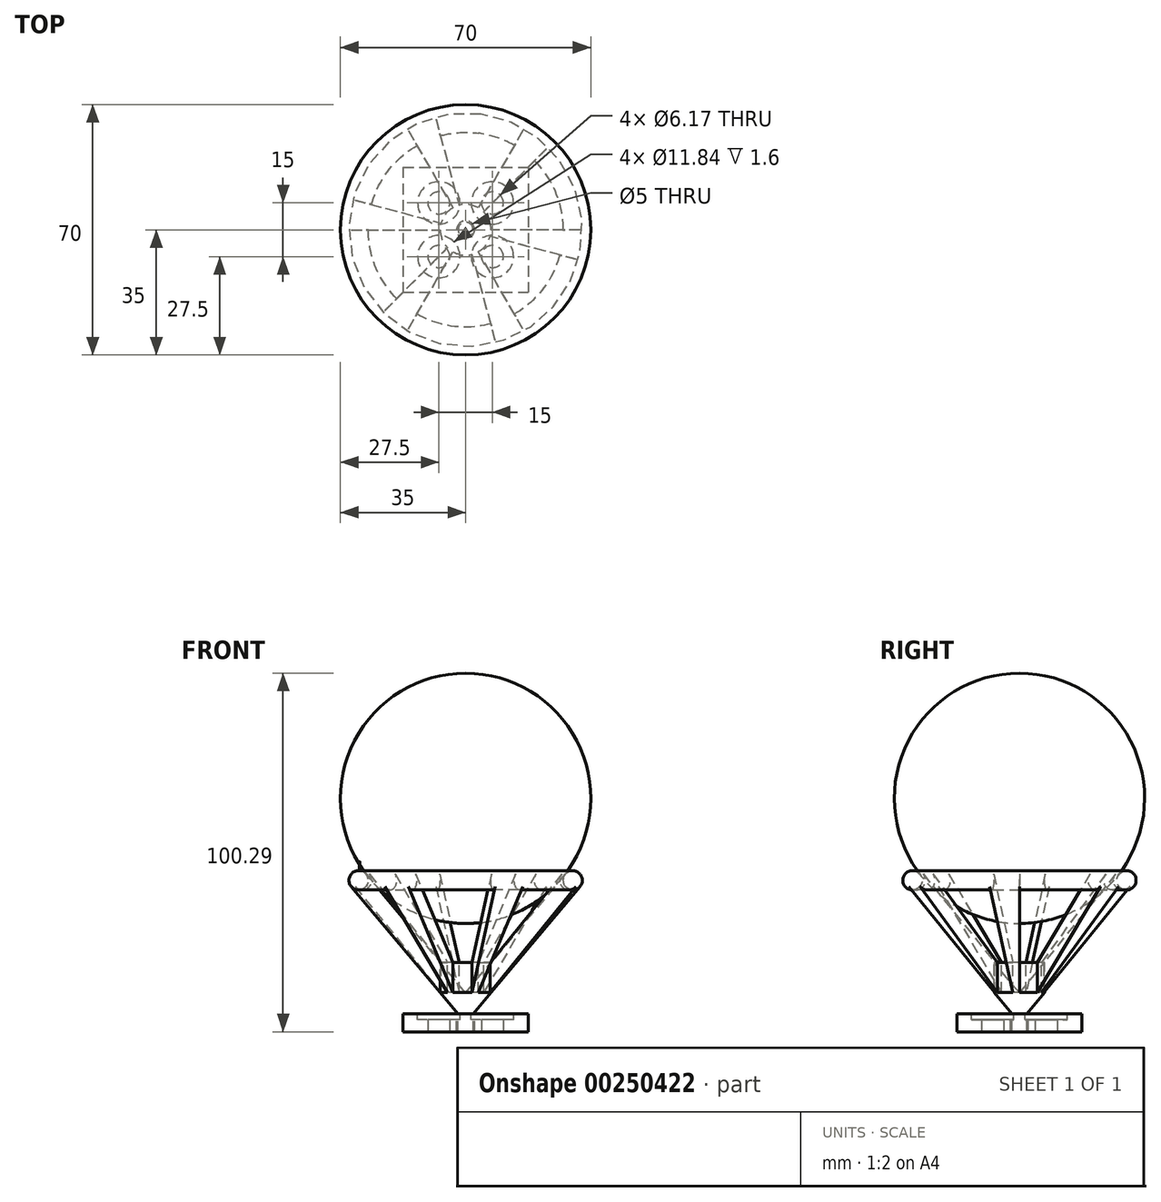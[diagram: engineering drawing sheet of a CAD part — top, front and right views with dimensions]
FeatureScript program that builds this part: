
annotation { "Feature Type Name" : "Feature", "Feature Type Description" : "" }
export const myFeature = defineFeature(function(context is Context, id is Id, definition is map)
    precondition{}
    {
        {
            var Q0;
            Q0=qCreatedBy(makeId("Top.planeOp"),FACE);
            var sketch = newSketch(context, id + "F0", { "sketchPlane" : qUnion([Q0])});
            skLineSegment(sketch, "E0.bottom", {"start": v(-17.5, 17.5) * mm, "end": v(0, 17.5) * mm});
            skLineSegment(sketch, "E0.top", {"start": v(-17.5, -17.5) * mm, "end": v(0, -17.5) * mm});
            skLineSegment(sketch, "E0.left", {"start": v(-17.5, 17.5) * mm, "end": v(-17.5, 0) * mm});
            skLineSegment(sketch, "E0.right", {"start": v(17.5, 17.5) * mm, "end": v(17.5, 0) * mm});
            skLineSegment(sketch, "E1", {"start": v(-17.5, 0) * mm, "end": v(-17.5, -17.5) * mm});
            skLineSegment(sketch, "E2", {"start": v(17.5, 0) * mm, "end": v(17.5, -17.5) * mm});
            skLineSegment(sketch, "E3", {"start": v(0, -17.5) * mm, "end": v(17.5, -17.5) * mm});
            skLineSegment(sketch, "E4", {"start": v(0, 17.5) * mm, "end": v(17.5, 17.5) * mm});
            skCircle(sketch, "E5", {"center": v(-7.5, 7.5) * mm, "radius": 3.09 * mm});
            skCircle(sketch, "E6", {"center": v(7.5, 7.5) * mm, "radius": 3.09 * mm});
            skLineSegment(sketch, "E7", {"start": v(-7.5, 7.5) * mm, "end": v(0, 7.5) * mm, "construction": true});
            skLineSegment(sketch, "E8", {"start": v(0, 7.5) * mm, "end": v(7.5, 7.5) * mm, "construction": true});
            skLineSegment(sketch, "E9", {"start": v(0, 7.5) * mm, "end": v(0, 0) * mm, "construction": true});
            skCircle(sketch, "E10.MirrorC", {"center": v(-7.5, -7.5) * mm, "radius": 3.09 * mm});
            skCircle(sketch, "E11.MirrorC", {"center": v(7.5, -7.5) * mm, "radius": 3.09 * mm});
            skSolve(sketch);
        }
        {
            var Q0;
            Q0 = qSketchRegion(id + "F0", true);
            extrude(context, id + "F1", {"entities" : qUnion([Q0]), "depth" : 5 * mm});
        }
        {
            var Q0;
            Q0=makeQuery(id+"F1.opExtrude","CAP_FACE",FACE,{"disambiguationData":[OSD([sQuery(id+"F0.wireOp",EDGE,"E0.bottom"),sQuery(id+"F0.wireOp",EDGE,"E0.top"),sQuery(id+"F0.wireOp",EDGE,"E0.left"),sQuery(id+"F0.wireOp",EDGE,"E0.right"),sQuery(id+"F0.wireOp",EDGE,"E1"),sQuery(id+"F0.wireOp",EDGE,"E2"),sQuery(id+"F0.wireOp",EDGE,"E3"),sQuery(id+"F0.wireOp",EDGE,"E4"),sQuery(id+"F0.wireOp",EDGE,"E5")])],"isStart":false});
            var sketch = newSketch(context, id + "F2", { "sketchPlane" : qUnion([Q0])});
            skCircle(sketch, "E12", {"center": v(-7.5, 7.5) * mm, "radius": 5.92 * mm});
            skCircle(sketch, "E13", {"center": v(7.5, 7.5) * mm, "radius": 5.92 * mm});
            skCircle(sketch, "E14.MirrorC", {"center": v(-7.5, -7.5) * mm, "radius": 5.92 * mm});
            skCircle(sketch, "E15.MirrorC", {"center": v(7.5, -7.5) * mm, "radius": 5.92 * mm});
            skSolve(sketch);
        }
        {
            var Q0;
            Q0 = qSketchRegion(id + "F2", true);
            extrude(context, id + "F3", {"entities" : qUnion([Q0]), "operationType" : NewBodyOperationType.REMOVE, "oppositeDirection" : true, "depth" : 1.6 * mm});
        }
        {
            var Q0;
            Q0=makeQuery(id+"F1.opExtrude","CAP_FACE",FACE,{"disambiguationData":[OSD([sQuery(id+"F0.wireOp",EDGE,"E0.bottom"),sQuery(id+"F0.wireOp",EDGE,"E0.top"),sQuery(id+"F0.wireOp",EDGE,"E0.left"),sQuery(id+"F0.wireOp",EDGE,"E0.right"),sQuery(id+"F0.wireOp",EDGE,"E1"),sQuery(id+"F0.wireOp",EDGE,"E2"),sQuery(id+"F0.wireOp",EDGE,"E3"),sQuery(id+"F0.wireOp",EDGE,"E4"),sQuery(id+"F0.wireOp",EDGE,"E5"),sQuery(id+"F0.wireOp",EDGE,"E6"),sQuery(id+"F0.wireOp",EDGE,"E10.MirrorC"),sQuery(id+"F0.wireOp",EDGE,"E11.MirrorC")])],"isStart":false});
            var sketch = newSketch(context, id + "F4", { "sketchPlane" : qUnion([Q0])});
            skCircle(sketch, "E16", {"center": v(0, 0) * mm, "radius": 2.5 * mm});
            skSolve(sketch);
        }
        {
            var Q0;
            Q0 = qSketchRegion(id + "F4", true);
            var Q1;
            Q1=makeQuery(id+"F1.opExtrude","CAP_FACE",FACE,{"disambiguationData":[OSD([sQuery(id+"F0.wireOp",EDGE,"E0.bottom"),sQuery(id+"F0.wireOp",EDGE,"E0.top"),sQuery(id+"F0.wireOp",EDGE,"E0.left"),sQuery(id+"F0.wireOp",EDGE,"E0.right"),sQuery(id+"F0.wireOp",EDGE,"E1"),sQuery(id+"F0.wireOp",EDGE,"E2"),sQuery(id+"F0.wireOp",EDGE,"E3"),sQuery(id+"F0.wireOp",EDGE,"E4"),sQuery(id+"F0.wireOp",EDGE,"E5"),sQuery(id+"F0.wireOp",EDGE,"E6"),sQuery(id+"F0.wireOp",EDGE,"E10.MirrorC"),sQuery(id+"F0.wireOp",EDGE,"E11.MirrorC")])],"isStart":true});
            extrude(context, id + "F5", {"entities" : qUnion([Q0]), "operationType" : NewBodyOperationType.REMOVE, "endBound" : BoundingType.UP_TO_SURFACE, "oppositeDirection" : true, "endBoundEntityFace" : qUnion([Q1]), "depth" : 25 * mm});
        }
        {
            var Q0;
            Q0=qCreatedBy(makeId("Front.planeOp"),FACE);
            var sketch = newSketch(context, id + "F6", { "sketchPlane" : qUnion([Q0])});
            skLineSegment(sketch, "E17.0", {"start": v(1.58, 5) * mm, "end": v(13.42, 5) * mm, "construction": true});
            skLineSegment(sketch, "E18.0", {"start": v(-13.42, 5) * mm, "end": v(-1.58, 5) * mm, "construction": true});
            skLineSegment(sketch, "E19", {"start": v(-1.58, 5) * mm, "end": v(-31.7, 40.9) * mm, "construction": true});
            skLineSegment(sketch, "E20", {"start": v(-27.87, 44.1) * mm, "end": v(0, 10.9) * mm});
            skLineSegment(sketch, "E21", {"start": v(0, 10.9) * mm, "end": v(0, 5) * mm});
            skLineSegment(sketch, "E22", {"start": v(0, 5) * mm, "end": v(-1.58, 5) * mm, "construction": true});
            skArc(sketch, "E23.converted", {"start": v(-27.87, 44.1) * mm, "mid": v(-31.39, 44.42) * mm, "end": v(-31.7, 40.9) * mm, "construction": true});
            skLineSegment(sketch, "E24.0", {"start": v(2.5, 0) * mm, "end": v(-2.5, 0) * mm, "construction": true});
            skLineSegment(sketch, "E25", {"start": v(-32, 40.64) * mm, "end": v(-2.1, 5) * mm});
            skLineSegment(sketch, "E26", {"start": v(-2.1, 5) * mm, "end": v(-2.1, 0) * mm});
            skLineSegment(sketch, "E27", {"start": v(-2.1, 0) * mm, "end": v(0, 0) * mm});
            skLineSegment(sketch, "E28", {"start": v(0, 0) * mm, "end": v(0, 5) * mm});
            skCircle(sketch, "E29", {"center": v(-29.93, 42.37) * mm, "radius": 2.7 * mm});
            skLineSegment(sketch, "E30", {"start": v(-27.87, 44.1) * mm, "end": v(-29.93, 42.37) * mm, "construction": true});
            skLineSegment(sketch, "E31", {"start": v(-29.78, 42.5) * mm, "end": v(-29.93, 42.37) * mm, "construction": true});
            skSolve(sketch);
        }
        {
            var Q0;
            Q0 = qSketchRegion(id + "F6", true);
            var Q1;
            Q1=sQuery(id+"F6.wireOp",EDGE,"E21");
            revolve(context, id + "F7", {"operationType" : NewBodyOperationType.ADD, "entities" : qUnion([Q0]), "axis" : qUnion([Q1]), "revolveType" : RevolveType.ONE_DIRECTION, "angle" : 15 * degree});
        }
        {
            var Q0;
            Q0=makeQuery(id+"F7.opRevolve","CAP_FACE",FACE,{"disambiguationData":[OSD([sQuery(id+"F6.wireOp",EDGE,"E20"),sQuery(id+"F6.wireOp",EDGE,"E21"),sQuery(id+"F6.wireOp",EDGE,"E25"),sQuery(id+"F6.wireOp",EDGE,"E26"),sQuery(id+"F6.wireOp",EDGE,"E27"),sQuery(id+"F6.wireOp",EDGE,"E28"),sQuery(id+"F6.wireOp",EDGE,"E29")])],"isStart":false});
            var sketch = newSketch(context, id + "F8", { "sketchPlane" : qUnion([Q0])});
            skLineSegment(sketch, "E32.0", {"start": v(0, 0) * mm, "end": v(0, 5) * mm});
            skLineSegment(sketch, "E32.1", {"start": v(2.1, 5) * mm, "end": v(2.1, 0) * mm});
            skLineSegment(sketch, "E32.3", {"start": v(0, 10.9) * mm, "end": v(0, 5) * mm});
            skLineSegment(sketch, "E32.4", {"start": v(7.1, 19.36) * mm, "end": v(0, 10.9) * mm});
            skLineSegment(sketch, "E32.5", {"start": v(7.1, 10.96) * mm, "end": v(2.1, 5) * mm});
            skLineSegment(sketch, "E33", {"start": v(7.1, 10.96) * mm, "end": v(7.1, 19.36) * mm});
            skCircle(sketch, "E34.converted", {"center": v(29.93, 42.37) * mm, "radius": 2.7 * mm});
            skPoint(sketch, "E35.orphan", {"position": v(27.87, 44.1) * mm});
            skPoint(sketch, "E36.orphan", {"position": v(32, 40.64) * mm});
            skLineSegment(sketch, "E37.0", {"start": v(2.1, 0) * mm, "end": v(0, 0) * mm});
            skSolve(sketch);
        }
        {
            var Q0;
            Q0 = qSketchRegion(id + "F8", true);
            var Q1;
            Q1=sQuery(id+"F8.wireOp",EDGE,"E32.3");
            revolve(context, id + "F9", {"operationType" : NewBodyOperationType.ADD, "entities" : qUnion([Q0]), "axis" : qUnion([Q1]), "revolveType" : RevolveType.ONE_DIRECTION, "angle" : 45 * degree});
        }
        {
            var Q0;
            Q0=makeQuery(id+"F7.opRevolve","SWEPT_BODY",BODY,{"disambiguationData":[OSD([sQuery(id+"F6.wireOp",EDGE,"E20"),sQuery(id+"F6.wireOp",EDGE,"E21"),sQuery(id+"F6.wireOp",EDGE,"E25"),sQuery(id+"F6.wireOp",EDGE,"E26"),sQuery(id+"F6.wireOp",EDGE,"E27"),sQuery(id+"F6.wireOp",EDGE,"E28"),sQuery(id+"F6.wireOp",EDGE,"E29")])]});
            var Q1;
            Q1=makeQuery(id+"F9.boolean.opBoolean","MERGE",EDGE,{"derivedFrom":[makeQuery(id+"F7.opRevolve","CAP_EDGE",EDGE,{"disambiguationData":[OSD([sQuery(id+"F6.wireOp",EDGE,"E21"),sQuery(id+"F6.wireOp",EDGE,"E28")])],"isStart":true}),makeQuery(id+"F9.opRevolve","CAP_EDGE",EDGE,{"disambiguationData":[OSD([sQuery(id+"F8.wireOp",EDGE,"E32.0"),sQuery(id+"F8.wireOp",EDGE,"E32.3")])],"isStart":true})]});
            circularPattern(context, id + "F10", {"entities" : qUnion([Q0]), "axis" : qUnion([Q1]), "angle" : 360 * degree, "instanceCount" : 6, "equalSpace" : true});
        }
        {
            var Q0;
            Q0=makeQuery(id+"F10.opPattern","COPY",BODY,{"derivedFrom":makeQuery(id+"F7.opRevolve","SWEPT_BODY",BODY,{"disambiguationData":[OSD([sQuery(id+"F6.wireOp",EDGE,"E20"),sQuery(id+"F6.wireOp",EDGE,"E21"),sQuery(id+"F6.wireOp",EDGE,"E25"),sQuery(id+"F6.wireOp",EDGE,"E26"),sQuery(id+"F6.wireOp",EDGE,"E27"),sQuery(id+"F6.wireOp",EDGE,"E28"),sQuery(id+"F6.wireOp",EDGE,"E29")])]}),"instanceName":"5"});
            var Q1;
            Q1=makeQuery(id+"F10.opPattern","COPY",BODY,{"derivedFrom":makeQuery(id+"F7.opRevolve","SWEPT_BODY",BODY,{"disambiguationData":[OSD([sQuery(id+"F6.wireOp",EDGE,"E20"),sQuery(id+"F6.wireOp",EDGE,"E21"),sQuery(id+"F6.wireOp",EDGE,"E25"),sQuery(id+"F6.wireOp",EDGE,"E26"),sQuery(id+"F6.wireOp",EDGE,"E27"),sQuery(id+"F6.wireOp",EDGE,"E28"),sQuery(id+"F6.wireOp",EDGE,"E29")])]}),"instanceName":"4"});
            var Q2;
            Q2=makeQuery(id+"F10.opPattern","COPY",BODY,{"derivedFrom":makeQuery(id+"F7.opRevolve","SWEPT_BODY",BODY,{"disambiguationData":[OSD([sQuery(id+"F6.wireOp",EDGE,"E20"),sQuery(id+"F6.wireOp",EDGE,"E21"),sQuery(id+"F6.wireOp",EDGE,"E25"),sQuery(id+"F6.wireOp",EDGE,"E26"),sQuery(id+"F6.wireOp",EDGE,"E27"),sQuery(id+"F6.wireOp",EDGE,"E28"),sQuery(id+"F6.wireOp",EDGE,"E29")])]}),"instanceName":"3"});
            var Q3;
            Q3=makeQuery(id+"F10.opPattern","COPY",BODY,{"derivedFrom":makeQuery(id+"F7.opRevolve","SWEPT_BODY",BODY,{"disambiguationData":[OSD([sQuery(id+"F6.wireOp",EDGE,"E20"),sQuery(id+"F6.wireOp",EDGE,"E21"),sQuery(id+"F6.wireOp",EDGE,"E25"),sQuery(id+"F6.wireOp",EDGE,"E26"),sQuery(id+"F6.wireOp",EDGE,"E27"),sQuery(id+"F6.wireOp",EDGE,"E28"),sQuery(id+"F6.wireOp",EDGE,"E29")])]}),"instanceName":"2"});
            var Q4;
            Q4=makeQuery(id+"F10.opPattern","COPY",BODY,{"derivedFrom":makeQuery(id+"F7.opRevolve","SWEPT_BODY",BODY,{"disambiguationData":[OSD([sQuery(id+"F6.wireOp",EDGE,"E20"),sQuery(id+"F6.wireOp",EDGE,"E21"),sQuery(id+"F6.wireOp",EDGE,"E25"),sQuery(id+"F6.wireOp",EDGE,"E26"),sQuery(id+"F6.wireOp",EDGE,"E27"),sQuery(id+"F6.wireOp",EDGE,"E28"),sQuery(id+"F6.wireOp",EDGE,"E29")])]}),"instanceName":"1"});
            var Q5;
            Q5=makeQuery(id+"F7.opRevolve","SWEPT_BODY",BODY,{"disambiguationData":[OSD([sQuery(id+"F6.wireOp",EDGE,"E20"),sQuery(id+"F6.wireOp",EDGE,"E21"),sQuery(id+"F6.wireOp",EDGE,"E25"),sQuery(id+"F6.wireOp",EDGE,"E26"),sQuery(id+"F6.wireOp",EDGE,"E27"),sQuery(id+"F6.wireOp",EDGE,"E28"),sQuery(id+"F6.wireOp",EDGE,"E29")])]});
            booleanBodies(context, id + "F11", {"operationType" : BooleanOperationType.UNION, "tools" : qUnion([Q0, Q1, Q2, Q3, Q4, Q5])});
        }
        {
            var Q0;
            Q0=qCreatedBy(makeId("Front.planeOp"),FACE);
            var sketch = newSketch(context, id + "F12", { "sketchPlane" : qUnion([Q0])});
            skArc(sketch, "E38", {"start": v(0, 100.29) * mm, "mid": v(-35, 65.29) * mm, "end": v(0, 30.29) * mm});
            skLineSegment(sketch, "E39", {"start": v(0, 30.29) * mm, "end": v(0, 100.29) * mm});
            skArc(sketch, "E40.0", {"start": v(-32, 40.64) * mm, "mid": v(-28.2, 40.3) * mm, "end": v(-27.87, 44.1) * mm, "construction": true});
            skSolve(sketch);
        }
        {
            var Q0;
            Q0 = qSketchRegion(id + "F12", true);
            var Q1;
            Q1=sQuery(id+"F12.wireOp",EDGE,"E39");
            revolve(context, id + "F13", {"entities" : qUnion([Q0]), "axis" : qUnion([Q1]), "revolveType" : RevolveType.FULL});
        }
    });
